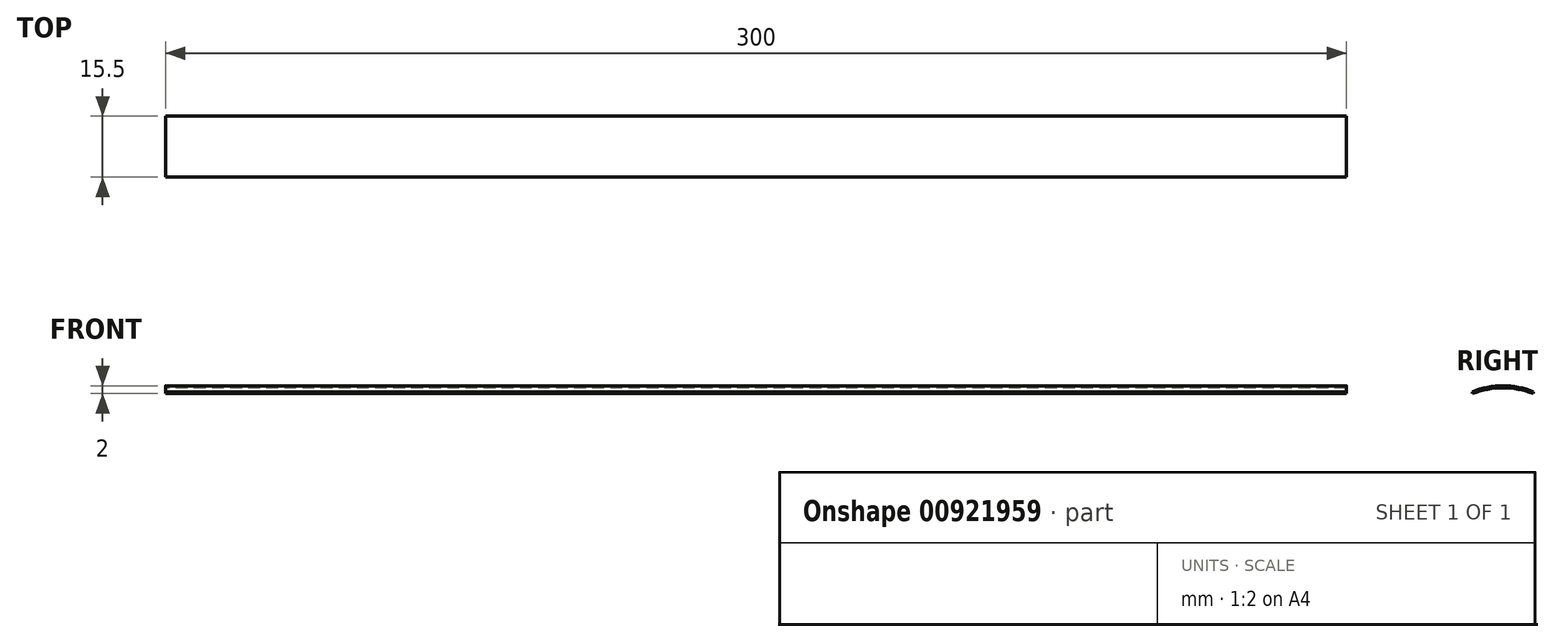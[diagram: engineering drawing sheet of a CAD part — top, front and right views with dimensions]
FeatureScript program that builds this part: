
annotation { "Feature Type Name" : "Feature", "Feature Type Description" : "" }
export const myFeature = defineFeature(function(context is Context, id is Id, definition is map)
    precondition{}
    {
        {
            var Q0;
            Q0=qCreatedBy(makeId("Right.planeOp"),FACE);
            var sketch = newSketch(context, id + "F0", { "sketchPlane" : qUnion([Q0])});
            skLineSegment(sketch, "E0.left", {"start": v(7.75, -1) * mm, "end": v(7.75, -0.5) * mm});
            skLineSegment(sketch, "E0.right", {"start": v(-7.75, -1) * mm, "end": v(-7.75, -0.5) * mm});
            skPoint(sketch, "E0.middle", {"position": v(0, 0) * mm});
            skLineSegment(sketch, "E1", {"start": v(0, 1) * mm, "end": v(0, 0.5) * mm});
            skPoint(sketch, "E2.orphan", {"position": v(-7.75, 1) * mm});
            skPoint(sketch, "E3.orphan", {"position": v(7.75, 1) * mm});
            skArc(sketch, "E4.trimOffspring", {"start": v(7.75, -0.5) * mm, "mid": v(0, 1) * mm, "end": v(-7.75, -0.5) * mm});
            skArc(sketch, "E5.trimOffspring", {"start": v(7.75, -1) * mm, "mid": v(0, 0.5) * mm, "end": v(-7.75, -1) * mm});
            skSolve(sketch);
        }
        {
            var Q0;
            Q0 = qSketchRegion(id + "F0", true);
            extrude(context, id + "F1", {"entities" : qUnion([Q0]), "depth" : 300 * mm, "offsetDistance" : 25 * mm});
        }
    });
